# Revit family: Toilet-Round-American_Standard-Evolution-2752XXX_Series
name_source: partatom
category: Plumbing Fixtures
units: mm (PartAtom-declared; Revit-internal decimal feet)

## family parameters
Always vertical = No
Cut with Voids When Loaded = No
OmniClass Number = 23.45.05.21.11.11
OmniClass Title = Water Operated Water Closets
Part Type = Normal
Room Calculation Point = No
Round Connector Dimension = Use Radius
Shared = Yes
Work Plane-Based = Yes

## types (2) — shared parameters
12" Rough In = Yes
3061 001 Round Front Universal Bowl = No
4061 813 Tank complete with trip lever located on right side = No
5282 011 Seat = No
5320 110 Seat = No
5322 019 Seat = No
Assembly Code = D2010110
Bowl Shape = Round
CW Connection = Yes
CWFU = 10
Cold Water Connection Diameter = 1/4"
Cold Water Connection Height = 10"
Cold Water Connection Radius = 1/8"
Cold Water Connection Width = 6"
Compliance Certifications = Meets or Exceeds the Following Specifications: • ASME A112.19.2-2008/CSA B45.1-08 for Vitreous China Fixtures • US EPA WaterSense HET’s
Default Elevation = 0"
Finish = Vitreous China-American Standard-020-White
Flush Rate = (1.28 gpf/4.8 Lpf)
HW Connection = No
Height = 28 3/8"
Installation Type = Floor Mounted
Length = 27 3/4"
Manufacturer = American Standard
Material = Vitreous China-American Standard-020-White
Product Documentation Link = https://americanstandard.box.com
Product Page URL = https://www.americanstandard.ca
Revised Date = 03/08/2023
Shipping Weight = 71.4 lbs (32.5 kg)
URL = http://www.americanstandard.ca
Vent Connection = No
WFU = 10
Warranty Information = Two-year warranty
Waste Connection = Yes
Waste Connection Diameter = 2"
Waste Connection Radius = 1"
Width = 18"
zero-valued in all types: HWFU

## per-type parameters (varying)
| type | 4061 128 Tank | 4061 513 Tank complete with Aquaguard Liner | Description |
| 2752513.020 | No | Yes | Evolution 2 Two-Piece 1.28 gpf/4.8 Lpf Standard Height Round Front Toilet Less Seat with Lined Tank |
| 2752128.020 | Yes | No | Evolution 2 Two-Piece 1.28 gpf/4.8 Lpf Standard Height Round Front Toilet Less Seat |

note: column(s) folded — value = type name in every type: Model

## geometry (parser evidence)
native form markers: Sweep x2
no freeform markers — native parametric forms only
